# Revit family: LH
name_source: partatom
category: Mechanical Equipment
units: mm (PartAtom-declared; Revit-internal decimal feet)

## family parameters
Always vertical = Yes
Cut with Voids When Loaded = No
Part Type = Normal
Room Calculation Point = No
Round Connector Dimension = Use Diameter
Shared = No
Work Plane-Based = No

## types (4) — shared parameters
Copper Pipes = Copper
DEPTH = 26 1/16"
Description = 3-Fan 2-Way Blow Evaporator
HEIGHT = 9 7/8"
Manufacturer = Krack Corporation
Revit Family Dates = 03/02/22SV
Type Comments = LH Series 3-Fan 2-Way Blow Evaporator
URL = www.krack.com

## per-type parameters (varying)
| type | 1 FAN | 2 FAN | 3 FAN | 4 FAN | LENGTH |
| LH4 | No | No | No | Yes | 98 7/8" |
| LH3 | No | No | Yes | No | 76 13/16" |
| LH2 | No | Yes | No | No | 54 13/16" |
| LH1 | Yes | No | No | No | 32 13/16" |

note: column(s) folded — value = type name in every type: Model

## geometry (parser evidence)
native form markers: Sweep x9
no freeform markers — native parametric forms only
